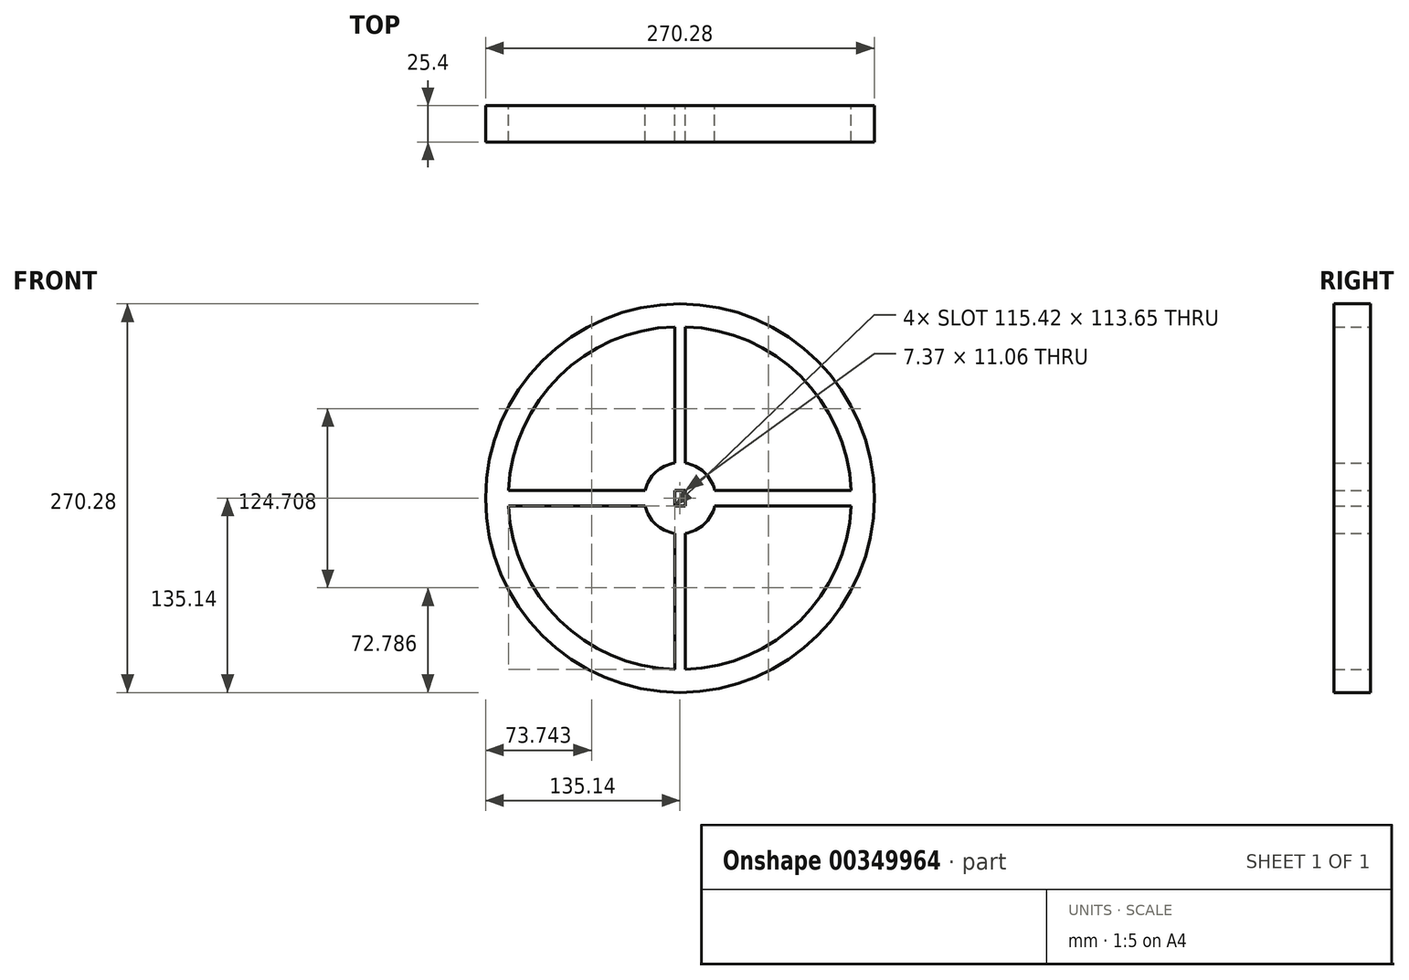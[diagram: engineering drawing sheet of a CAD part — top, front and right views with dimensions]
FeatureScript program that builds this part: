
annotation { "Feature Type Name" : "Feature", "Feature Type Description" : "" }
export const myFeature = defineFeature(function(context is Context, id is Id, definition is map)
    precondition{}
    {
        {
            var Q0;
            Q0=qCreatedBy(makeId("Front.planeOp"),FACE);
            var sketch = newSketch(context, id + "F0", { "sketchPlane" : qUnion([Q0])});
            skCircle(sketch, "E0", {"center": v(0, 0) * mm, "radius": 135.14 * mm});
            skCircle(sketch, "E1", {"center": v(0, 0) * mm, "radius": 119.24 * mm});
            skSolve(sketch);
        }
        {
            var Q0;
            Q0 = qSketchRegion(id + "F0", true);
            extrude(context, id + "F1", {"entities" : qUnion([Q0]), "depth" : 25.4 * mm});
        }
        {
            var Q0;
            Q0=qCreatedBy(makeId("Front.planeOp"),FACE);
            var sketch = newSketch(context, id + "F2", { "sketchPlane" : qUnion([Q0])});
            skCircle(sketch, "E2", {"center": v(0, 0) * mm, "radius": 24.72 * mm});
            skLineSegment(sketch, "E3.bottom", {"start": v(3.69, 119.32) * mm, "end": v(-3.69, 119.32) * mm});
            skLineSegment(sketch, "E3.top", {"start": v(3.69, -119.32) * mm, "end": v(-3.69, -119.32) * mm});
            skLineSegment(sketch, "E3.left", {"start": v(3.69, 119.32) * mm, "end": v(3.69, -119.32) * mm});
            skLineSegment(sketch, "E3.right", {"start": v(-3.69, 119.32) * mm, "end": v(-3.69, -119.32) * mm});
            skLineSegment(sketch, "E4.bottom", {"start": v(120.7, -5.53) * mm, "end": v(-120.7, -5.53) * mm});
            skLineSegment(sketch, "E4.top", {"start": v(120.7, 5.53) * mm, "end": v(-120.7, 5.53) * mm});
            skLineSegment(sketch, "E4.left", {"start": v(120.7, -5.53) * mm, "end": v(120.7, 5.53) * mm});
            skLineSegment(sketch, "E4.right", {"start": v(-120.7, -5.53) * mm, "end": v(-120.7, 5.53) * mm});
            skSolve(sketch);
        }
        {
            var Q0;
            Q0 = qSketchRegion(id + "F2", true);
            extrude(context, id + "F3", {"entities" : qUnion([Q0]), "operationType" : NewBodyOperationType.ADD, "depth" : 25.4 * mm});
        }
    });
